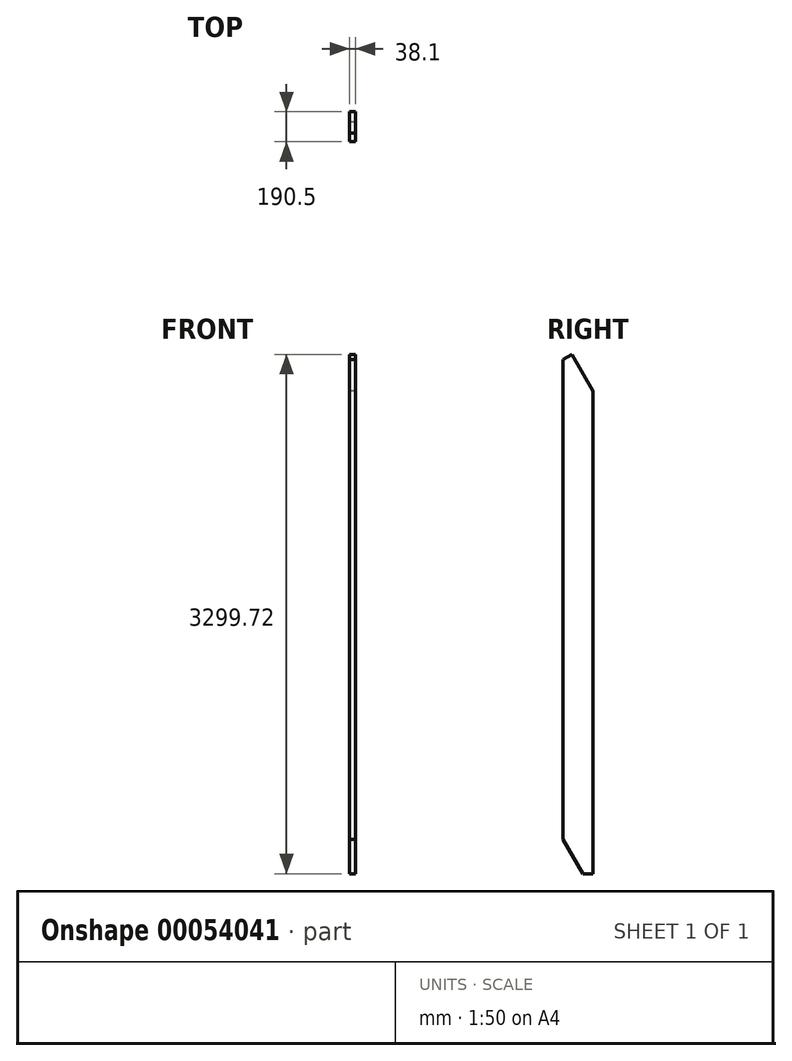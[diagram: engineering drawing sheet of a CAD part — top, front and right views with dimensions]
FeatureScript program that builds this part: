
annotation { "Feature Type Name" : "Feature", "Feature Type Description" : "" }
export const myFeature = defineFeature(function(context is Context, id is Id, definition is map)
    precondition{}
    {
        {
            var Q0;
            Q0=qCreatedBy(makeId("Right.planeOp"),FACE);
            var sketch = newSketch(context, id + "F0", { "sketchPlane" : qUnion([Q0])});
            skLineSegment(sketch, "E0", {"start": v(0, 0) * mm, "end": v(-190.5, 329.96) * mm});
            skLineSegment(sketch, "E1", {"start": v(-190.5, 329.96) * mm, "end": v(-190.5, 3504.96) * mm});
            skLineSegment(sketch, "E2", {"start": v(-190.5, 3504.96) * mm, "end": v(0, 3175) * mm});
            skLineSegment(sketch, "E3", {"start": v(0, 3175) * mm, "end": v(0, 0) * mm});
            skSolve(sketch);
        }
        {
            var Q0;
            Q0=makeQuery(id+"F0.imprint","IMPRINT",FACE,{"disambiguationData":[TD([[makeQuery(id+"F0.imprint","IMPRINT",EDGE,{"derivedFrom":sQuery(id+"F0.wireOp",EDGE,"E0")}),-1.0]])]});
            extrude(context, id + "F1", {"entities" : qUnion([Q0]), "depth" : 38.1 * mm});
        }
        {
            var Q0;
            Q0=makeQuery(id+"F1.opExtrude","SWEPT_EDGE",EDGE,{"disambiguationData":[OSD([sQuery(id+"F0.wireOp",EDGE,"E0"),sQuery(id+"F0.wireOp",EDGE,"E3")])]});
            chamfer(context, id + "F2", {"entities" : qUnion([Q0]), "chamferType" : ChamferType.OFFSET_ANGLE, "width" : 127 * mm, "oppositeDirection" : false, "angle" : 60 * degree, "tangentPropagation" : true});
        }
        {
            var Q0;
            Q0=makeQuery(id+"F1.opExtrude","SWEPT_EDGE",EDGE,{"disambiguationData":[OSD([sQuery(id+"F0.wireOp",EDGE,"E1"),sQuery(id+"F0.wireOp",EDGE,"E2")])]});
            chamfer(context, id + "F3", {"entities" : qUnion([Q0]), "chamferType" : ChamferType.OFFSET_ANGLE, "width" : 127 * mm, "oppositeDirection" : false, "angle" : 60 * degree, "tangentPropagation" : true});
        }
    });
